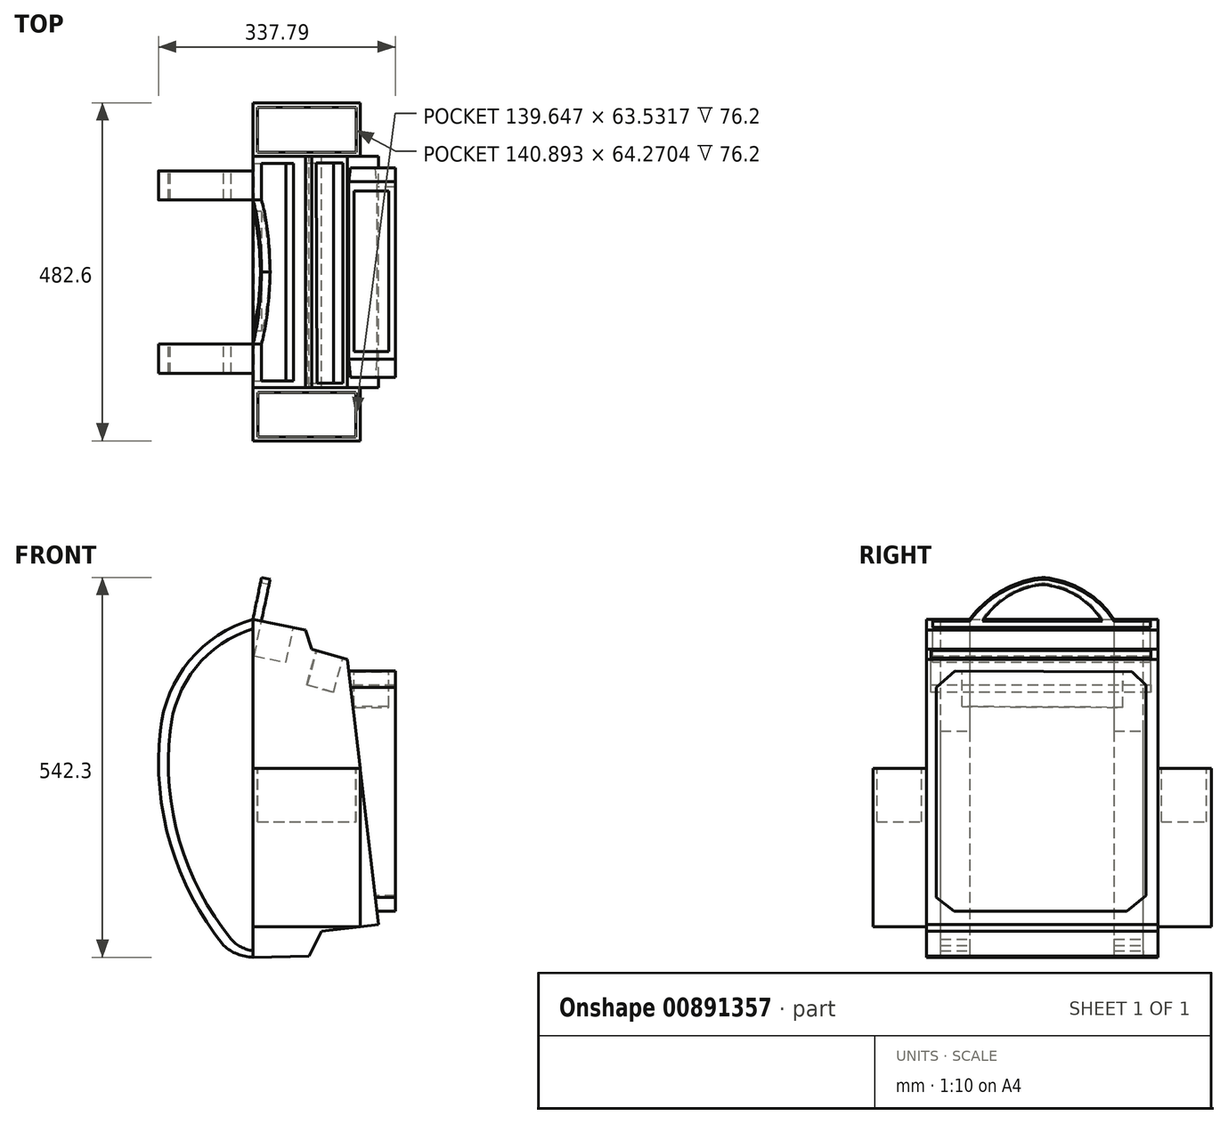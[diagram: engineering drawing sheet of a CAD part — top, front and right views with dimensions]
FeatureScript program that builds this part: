
annotation { "Feature Type Name" : "Feature", "Feature Type Description" : "" }
export const myFeature = defineFeature(function(context is Context, id is Id, definition is map)
    precondition{}
    {
        {
            var Q0;
            Q0=qCreatedBy(makeId("Front.planeOp"),FACE);
            var sketch = newSketch(context, id + "F0", { "sketchPlane" : qUnion([Q0])});
            skLineSegment(sketch, "E0", {"start": v(0, 290.27) * mm, "end": v(0, -192.33) * mm});
            skLineSegment(sketch, "E1", {"start": v(0, 290.27) * mm, "end": v(75.03, 274.73) * mm});
            skLineSegment(sketch, "E2", {"start": v(75.03, 274.73) * mm, "end": v(83.63, 247.47) * mm});
            skLineSegment(sketch, "E3", {"start": v(83.63, 247.47) * mm, "end": v(134.57, 233.12) * mm});
            skLineSegment(sketch, "E4", {"start": v(134.57, 233.12) * mm, "end": v(179.05, -145.66) * mm});
            skLineSegment(sketch, "E5", {"start": v(179.05, -145.66) * mm, "end": v(97.75, -155.2) * mm});
            skLineSegment(sketch, "E6", {"start": v(97.75, -155.2) * mm, "end": v(80.05, -190.86) * mm});
            skLineSegment(sketch, "E7", {"start": v(80.05, -190.86) * mm, "end": v(0, -192.33) * mm});
            skSolve(sketch);
        }
        {
            var Q0;
            Q0 = qSketchRegion(id + "F0", true);
            extrude(context, id + "F1", {"entities" : qUnion([Q0]), "depth" : 330.2 * mm, "offsetDistance" : 25.4 * mm});
        }
        {
            var Q0;
            Q0=qCreatedBy(makeId("Right.planeOp"),FACE);
            var sketch = newSketch(context, id + "F2", { "sketchPlane" : qUnion([Q0])});
            skLineSegment(sketch, "E8", {"start": v(-289.58, 216.38) * mm, "end": v(-316.12, 192.85) * mm});
            skLineSegment(sketch, "E9", {"start": v(-316.12, 192.85) * mm, "end": v(-316.12, -106.97) * mm});
            skLineSegment(sketch, "E10", {"start": v(-316.12, -106.97) * mm, "end": v(-290.78, -126.27) * mm});
            skLineSegment(sketch, "E11", {"start": v(-290.78, -126.27) * mm, "end": v(-44.05, -126.27) * mm});
            skLineSegment(sketch, "E12", {"start": v(-44.05, -126.27) * mm, "end": v(-16.9, -104.55) * mm});
            skLineSegment(sketch, "E13", {"start": v(-16.9, -104.55) * mm, "end": v(-16.9, 195.87) * mm});
            skLineSegment(sketch, "E14", {"start": v(-16.9, 195.87) * mm, "end": v(-36.81, 215.17) * mm});
            skLineSegment(sketch, "E15", {"start": v(-36.81, 215.17) * mm, "end": v(-289.58, 216.38) * mm});
            skSolve(sketch);
        }
        {
            var Q0;
            Q0 = qSketchRegion(id + "F2", true);
            extrude(context, id + "F3", {"entities" : qUnion([Q0]), "operationType" : NewBodyOperationType.ADD, "depth" : 203.2 * mm, "offsetDistance" : 25.4 * mm});
        }
        {
            var Q0;
            Q0=qCreatedBy(makeId("Right.planeOp"),FACE);
            var sketch = newSketch(context, id + "F4", { "sketchPlane" : qUnion([Q0])});
            skLineSegment(sketch, "E16", {"start": v(-20.96, 291.52) * mm, "end": v(-62.57, 291.52) * mm});
            skLineSegment(sketch, "E17", {"start": v(-62.57, 291.52) * mm, "end": v(-62.57, -192) * mm});
            skLineSegment(sketch, "E18", {"start": v(-62.57, -192) * mm, "end": v(-26.7, -192) * mm});
            skLineSegment(sketch, "E19", {"start": v(-20.96, 291.52) * mm, "end": v(-20.96, -192) * mm});
            skLineSegment(sketch, "E20", {"start": v(-20.96, -192) * mm, "end": v(-26.7, -192) * mm});
            skLineSegment(sketch, "E21", {"start": v(-309.94, 291.52) * mm, "end": v(-268.38, 291.52) * mm});
            skLineSegment(sketch, "E22", {"start": v(-268.38, 291.52) * mm, "end": v(-268.38, -192) * mm});
            skLineSegment(sketch, "E23", {"start": v(-268.38, -192) * mm, "end": v(-309.94, -192) * mm});
            skLineSegment(sketch, "E24", {"start": v(-309.94, -192) * mm, "end": v(-309.94, 291.52) * mm});
            skPoint(sketch, "E25.start.orphan", {"position": v(-330.88, 291.52) * mm});
            skSolve(sketch);
        }
        {
            var Q0;
            Q0 = qSketchRegion(id + "F4", true);
            extrude(context, id + "F5", {"entities" : qUnion([Q0]), "operationType" : NewBodyOperationType.ADD, "oppositeDirection" : true, "depth" : 139.7 * mm, "offsetDistance" : 25.4 * mm});
        }
        {
            var Q0;
            Q0=makeQuery(id+"F5.opExtrude","SWEPT_FACE",FACE,{"disambiguationData":[OSD([sQuery(id+"F4.wireOp",EDGE,"E19")])]});
            var sketch = newSketch(context, id + "F6", { "sketchPlane" : qUnion([Q0])});
            skArc(sketch, "E26", {"start": v(132.19, 131.03) * mm, "mid": v(90.38, 230.81) * mm, "end": v(0, 290.27) * mm});
            skArc(sketch, "E27", {"start": v(41.56, -175.37) * mm, "mid": v(117.54, -31.24) * mm, "end": v(132.19, 131.03) * mm});
            skArc(sketch, "E28", {"start": v(0, -192) * mm, "mid": v(22.38, -187.68) * mm, "end": v(41.56, -175.37) * mm});
            skSolve(sketch);
        }
        {
            var Q0;
            Q0=makeQuery(id+"F6.imprint","IMPRINT",FACE,{"disambiguationData":[TD([[makeQuery(id+"F6.imprint","IMPRINT",EDGE,{"derivedFrom":sQuery(id+"F6.wireOp",EDGE,"E26")}),-1.0]])]});
            var sketch = newSketch(context, id + "F7", { "sketchPlane" : qUnion([Q0])});
            skArc(sketch, "E29", {"start": v(117.94, 130.34) * mm, "mid": v(81.32, 221.54) * mm, "end": v(0, 276.7) * mm});
            skArc(sketch, "E30", {"start": v(30.85, -166.62) * mm, "mid": v(104.4, -26.94) * mm, "end": v(117.94, 130.34) * mm});
            skArc(sketch, "E31", {"start": v(0, -182.95) * mm, "mid": v(16.9, -177.58) * mm, "end": v(30.85, -166.62) * mm});
            skLineSegment(sketch, "E32", {"start": v(0, 276.7) * mm, "end": v(0, -182.95) * mm});
            skSolve(sketch);
        }
        {
            var Q0;
            Q0=makeQuery(id+"F7.imprint","IMPRINT",FACE,{"disambiguationData":[TD([[makeQuery(id+"F7.imprint","IMPRINT",EDGE,{"derivedFrom":makeQuery(id+"F6.imprint","IMPRINT",EDGE,{"derivedFrom":sQuery(id+"F6.wireOp",EDGE,"E26")})}),-1.0]])]});
            extrude(context, id + "F8", {"entities" : qUnion([Q0]), "operationType" : NewBodyOperationType.REMOVE, "oppositeDirection" : true, "depth" : 304.8 * mm, "offsetDistance" : 25.4 * mm});
        }
        {
            var Q0;
            Q0 = qSketchRegion(id + "F7", true);
            extrude(context, id + "F9", {"entities" : qUnion([Q0]), "operationType" : NewBodyOperationType.REMOVE, "oppositeDirection" : true, "depth" : 304.8 * mm, "offsetDistance" : 25.4 * mm});
        }
        {
            var Q0;
            Q0=makeQuery(id+"F1.opExtrude","SWEPT_FACE",FACE,{"disambiguationData":[OSD([sQuery(id+"F0.wireOp",EDGE,"E1")])]});
            var sketch = newSketch(context, id + "F10", { "sketchPlane" : qUnion([Q0])});
            skLineSegment(sketch, "E33", {"start": v(-44.36, -10.48) * mm, "end": v(0, -10.48) * mm});
            skPoint(sketch, "E33.startSnap0", {"position": v(-58.89, -10.48) * mm});
            skLineSegment(sketch, "E34", {"start": v(0, -10.48) * mm, "end": v(0, -320.8) * mm});
            skLineSegment(sketch, "E35", {"start": v(0, -320.8) * mm, "end": v(-46.44, -320.8) * mm});
            skLineSegment(sketch, "E36", {"start": v(-46.44, -320.8) * mm, "end": v(-46.44, -10.48) * mm});
            skLineSegment(sketch, "E37", {"start": v(-44.36, -10.48) * mm, "end": v(-46.44, -10.48) * mm});
            skSolve(sketch);
        }
        {
            var Q0;
            Q0=makeQuery(id+"F1.opExtrude","SWEPT_FACE",FACE,{"disambiguationData":[OSD([sQuery(id+"F0.wireOp",EDGE,"E3")])]});
            var sketch = newSketch(context, id + "F11", { "sketchPlane" : qUnion([Q0])});
            skLineSegment(sketch, "E38", {"start": v(20.46, -9.9) * mm, "end": v(60.04, -9.9) * mm});
            skLineSegment(sketch, "E39", {"start": v(60.04, -9.9) * mm, "end": v(60.04, -323.85) * mm});
            skLineSegment(sketch, "E40", {"start": v(60.04, -323.85) * mm, "end": v(21.51, -323.85) * mm});
            skLineSegment(sketch, "E41", {"start": v(21.51, -323.85) * mm, "end": v(20.46, -9.9) * mm});
            skSolve(sketch);
        }
        {
            var Q0;
            Q0=makeQuery(id+"F3.opExtrude","SWEPT_FACE",FACE,{"disambiguationData":[OSD([sQuery(id+"F2.wireOp",EDGE,"E15")])]});
            var sketch = newSketch(context, id + "F12", { "sketchPlane" : qUnion([Q0])});
            skLineSegment(sketch, "E42", {"start": v(145.8, -50.56) * mm, "end": v(193.55, -50.58) * mm});
            skLineSegment(sketch, "E43", {"start": v(193.55, -50.58) * mm, "end": v(193.55, -280.18) * mm});
            skLineSegment(sketch, "E44", {"start": v(193.55, -280.18) * mm, "end": v(144.27, -280.18) * mm});
            skLineSegment(sketch, "E45", {"start": v(144.27, -280.18) * mm, "end": v(144.27, -50.56) * mm});
            skLineSegment(sketch, "E46", {"start": v(144.27, -50.56) * mm, "end": v(145.8, -50.56) * mm});
            skSolve(sketch);
        }
        {
            var Q0;
            Q0 = qSketchRegion(id + "F12", true);
            extrude(context, id + "F13", {"entities" : qUnion([Q0]), "operationType" : NewBodyOperationType.REMOVE, "oppositeDirection" : true, "depth" : 50.8 * mm, "offsetDistance" : 25.4 * mm});
        }
        {
            var Q0;
            Q0=makeQuery(id+"F10.imprint","IMPRINT",FACE,{"disambiguationData":[TD([[makeQuery(id+"F10.imprint","IMPRINT",EDGE,{"derivedFrom":sQuery(id+"F10.wireOp",EDGE,"E33")}),-1.0]])]});
            extrude(context, id + "F14", {"entities" : qUnion([Q0]), "operationType" : NewBodyOperationType.REMOVE, "oppositeDirection" : true, "depth" : 50.8 * mm, "offsetDistance" : 25.4 * mm});
        }
        {
            var Q0;
            Q0=makeQuery(id+"F11.imprint","IMPRINT",FACE,{"disambiguationData":[TD([[makeQuery(id+"F11.imprint","IMPRINT",EDGE,{"derivedFrom":sQuery(id+"F11.wireOp",EDGE,"E38")}),-1.0]])]});
            extrude(context, id + "F15", {"entities" : qUnion([Q0]), "operationType" : NewBodyOperationType.REMOVE, "oppositeDirection" : true, "depth" : 50.8 * mm, "offsetDistance" : 25.4 * mm});
        }
        {
            var Q0;
            Q0=makeQuery(id+"F1.opExtrude","SWEPT_FACE",FACE,{"disambiguationData":[OSD([sQuery(id+"F0.wireOp",EDGE,"E1")])]});
            var sketch = newSketch(context, id + "F16", { "sketchPlane" : qUnion([Q0])});
            skLineSegment(sketch, "E47", {"start": v(-58.89, -62.57) * mm, "end": v(-58.89, -268.38) * mm});
            skLineSegment(sketch, "E48", {"start": v(-58.89, -268.38) * mm, "end": v(-46.44, -268.38) * mm});
            skLineSegment(sketch, "E49", {"start": v(-46.44, -268.38) * mm, "end": v(-46.44, -62.57) * mm});
            skLineSegment(sketch, "E50", {"start": v(-46.44, -62.57) * mm, "end": v(-58.89, -62.57) * mm});
            skSolve(sketch);
        }
        {
            var Q0;
            Q0 = qSketchRegion(id + "F16", true);
            extrude(context, id + "F17", {"entities" : qUnion([Q0]), "operationType" : NewBodyOperationType.ADD, "depth" : 60.96 * mm, "offsetDistance" : 25.4 * mm});
        }
        {
            var Q0;
            Q0=makeQuery(id+"F17.opExtrude","SWEPT_FACE",FACE,{"disambiguationData":[OSD([sQuery(id+"F16.wireOp",EDGE,"E47")])]});
            var sketch = newSketch(context, id + "F18", { "sketchPlane" : qUnion([Q0])});
            skArc(sketch, "E51", {"start": v(165.48, 345.2) * mm, "mid": v(106.82, 326.88) * mm, "end": v(62.57, 284.24) * mm});
            skArc(sketch, "E52", {"start": v(268.38, 284.24) * mm, "mid": v(223.26, 325.41) * mm, "end": v(165.48, 345.2) * mm});
            skArc(sketch, "E53", {"start": v(249.73, 284.24) * mm, "mid": v(213.66, 320.42) * mm, "end": v(165.48, 337.4) * mm});
            skArc(sketch, "E54", {"start": v(165.48, 337.4) * mm, "mid": v(115.97, 321.25) * mm, "end": v(79.33, 284.24) * mm});
            skLineSegment(sketch, "E55", {"start": v(62.57, 284.24) * mm, "end": v(268.38, 284.24) * mm});
            skSolve(sketch);
        }
        {
            var Q0;
            {var subQ0=sQuery(id+"F18.wireOp",EDGE,"E51");Q0=makeQuery(id+"F18.imprint","IMPRINT",FACE,{"disambiguationData":[TD([[makeQuery(id+"F18.imprint","IMPRINT",EDGE,{"derivedFrom":subQ0}),-1.0]])]});}
            var Q1;
            {var subQ0=sQuery(id+"F18.wireOp",EDGE,"E52");Q1=makeQuery(id+"F18.imprint","IMPRINT",FACE,{"disambiguationData":[TD([[makeQuery(id+"F18.imprint","IMPRINT",EDGE,{"derivedFrom":subQ0}),-1.0]])]});}
            extrude(context, id + "F19", {"entities" : qUnion([Q0, Q1]), "operationType" : NewBodyOperationType.REMOVE, "oppositeDirection" : true, "depth" : 25.4 * mm, "offsetDistance" : 25.4 * mm});
        }
        {
            var Q0;
            {var subQ0=sQuery(id+"F18.wireOp",EDGE,"E53");Q0=makeQuery(id+"F18.imprint","IMPRINT",FACE,{"disambiguationData":[TD([[makeQuery(id+"F18.imprint","IMPRINT",EDGE,{"derivedFrom":subQ0}),1.0]])]});}
            extrude(context, id + "F20", {"entities" : qUnion([Q0]), "operationType" : NewBodyOperationType.REMOVE, "oppositeDirection" : true, "depth" : 25.4 * mm, "offsetDistance" : 25.4 * mm});
        }
        {
            var Q0;
            Q0=makeQuery(id+"F1.opExtrude","CAP_FACE",FACE,{"disambiguationData":[OSD([sQuery(id+"F0.wireOp",EDGE,"E0"),sQuery(id+"F0.wireOp",EDGE,"E1"),sQuery(id+"F0.wireOp",EDGE,"E2"),sQuery(id+"F0.wireOp",EDGE,"E3"),sQuery(id+"F0.wireOp",EDGE,"E4"),sQuery(id+"F0.wireOp",EDGE,"E5"),sQuery(id+"F0.wireOp",EDGE,"E6"),sQuery(id+"F0.wireOp",EDGE,"E7")])],"isStart":true});
            var sketch = newSketch(context, id + "F21", { "sketchPlane" : qUnion([Q0])});
            skLineSegment(sketch, "E56.bottom", {"start": v(0, 77) * mm, "end": v(-153.17, 77) * mm});
            skLineSegment(sketch, "E56.top", {"start": v(0, -148.7) * mm, "end": v(-153.17, -148.7) * mm});
            skLineSegment(sketch, "E56.left", {"start": v(0, 77) * mm, "end": v(0, -148.7) * mm});
            skLineSegment(sketch, "E56.right", {"start": v(-153.17, 77) * mm, "end": v(-153.17, -148.7) * mm});
            skSolve(sketch);
        }
        {
            var Q0;
            Q0 = qSketchRegion(id + "F21", true);
            extrude(context, id + "F22", {"entities" : qUnion([Q0]), "operationType" : NewBodyOperationType.ADD, "depth" : 76.2 * mm, "offsetDistance" : 25.4 * mm});
        }
        {
            var Q0;
            Q0=makeQuery(id+"F1.opExtrude","CAP_FACE",FACE,{"disambiguationData":[OSD([sQuery(id+"F0.wireOp",EDGE,"E0"),sQuery(id+"F0.wireOp",EDGE,"E1"),sQuery(id+"F0.wireOp",EDGE,"E2"),sQuery(id+"F0.wireOp",EDGE,"E3"),sQuery(id+"F0.wireOp",EDGE,"E4"),sQuery(id+"F0.wireOp",EDGE,"E5"),sQuery(id+"F0.wireOp",EDGE,"E6"),sQuery(id+"F0.wireOp",EDGE,"E7")])],"isStart":false});
            var sketch = newSketch(context, id + "F23", { "sketchPlane" : qUnion([Q0])});
            skLineSegment(sketch, "E57.bottom", {"start": v(0, 77) * mm, "end": v(153.08, 77) * mm});
            skLineSegment(sketch, "E57.top", {"start": v(0, -148.7) * mm, "end": v(153.08, -148.7) * mm});
            skLineSegment(sketch, "E57.left", {"start": v(0, 77) * mm, "end": v(0, -148.7) * mm});
            skLineSegment(sketch, "E57.right", {"start": v(153.08, 77) * mm, "end": v(153.08, -148.7) * mm});
            skSolve(sketch);
        }
        {
            var Q0;
            Q0 = qSketchRegion(id + "F23", true);
            extrude(context, id + "F24", {"entities" : qUnion([Q0]), "operationType" : NewBodyOperationType.ADD, "depth" : 76.2 * mm, "offsetDistance" : 25.4 * mm});
        }
        {
            var Q0;
            Q0=makeQuery(id+"F24.opExtrude","SWEPT_FACE",FACE,{"disambiguationData":[OSD([sQuery(id+"F23.wireOp",EDGE,"E57.bottom")])]});
            var sketch = newSketch(context, id + "F25", { "sketchPlane" : qUnion([Q0])});
            skLineSegment(sketch, "E58.bottom", {"start": v(7.22, -400.75) * mm, "end": v(146.87, -400.75) * mm});
            skLineSegment(sketch, "E58.top", {"start": v(7.22, -337.22) * mm, "end": v(146.87, -337.22) * mm});
            skLineSegment(sketch, "E58.left", {"start": v(7.22, -400.75) * mm, "end": v(7.22, -337.22) * mm});
            skLineSegment(sketch, "E58.right", {"start": v(146.87, -400.75) * mm, "end": v(146.87, -337.22) * mm});
            skSolve(sketch);
        }
        {
            var Q0;
            Q0=makeQuery(id+"F25.imprint","IMPRINT",FACE,{"disambiguationData":[TD([[makeQuery(id+"F25.imprint","IMPRINT",EDGE,{"derivedFrom":sQuery(id+"F25.wireOp",EDGE,"E58.bottom")}),1.0]])]});
            extrude(context, id + "F26", {"entities" : qUnion([Q0]), "operationType" : NewBodyOperationType.REMOVE, "oppositeDirection" : true, "depth" : 76.2 * mm, "offsetDistance" : 25.4 * mm});
        }
        {
            var Q0;
            Q0=makeQuery(id+"F22.opExtrude","SWEPT_FACE",FACE,{"disambiguationData":[OSD([sQuery(id+"F21.wireOp",EDGE,"E56.bottom")])]});
            var sketch = newSketch(context, id + "F27", { "sketchPlane" : qUnion([Q0])});
            skLineSegment(sketch, "E59.bottom", {"start": v(-121.5, -332.95) * mm, "end": v(-113.1, -332.95) * mm});
            skLineSegment(sketch, "E59.top", {"start": v(-121.5, -312.3) * mm, "end": v(-113.1, -312.3) * mm});
            skLineSegment(sketch, "E59.left", {"start": v(-121.5, -332.95) * mm, "end": v(-121.5, -312.3) * mm});
            skLineSegment(sketch, "E59.right", {"start": v(-113.1, -332.95) * mm, "end": v(-113.1, -312.3) * mm});
            skLineSegment(sketch, "E60.bottom", {"start": v(6.24, 5.18) * mm, "end": v(147.13, 5.18) * mm});
            skLineSegment(sketch, "E60.top", {"start": v(6.24, 69.45) * mm, "end": v(147.13, 69.45) * mm});
            skLineSegment(sketch, "E60.left", {"start": v(6.24, 5.18) * mm, "end": v(6.24, 69.45) * mm});
            skLineSegment(sketch, "E60.right", {"start": v(147.13, 5.18) * mm, "end": v(147.13, 69.45) * mm});
            skSolve(sketch);
        }
        {
            var Q0;
            Q0=makeQuery(id+"F27.imprint","IMPRINT",FACE,{"disambiguationData":[TD([[makeQuery(id+"F27.imprint","IMPRINT",EDGE,{"derivedFrom":sQuery(id+"F27.wireOp",EDGE,"E60.bottom")}),1.0]])]});
            extrude(context, id + "F28", {"entities" : qUnion([Q0]), "operationType" : NewBodyOperationType.REMOVE, "oppositeDirection" : true, "depth" : 76.2 * mm, "offsetDistance" : 25.4 * mm});
        }
    });
